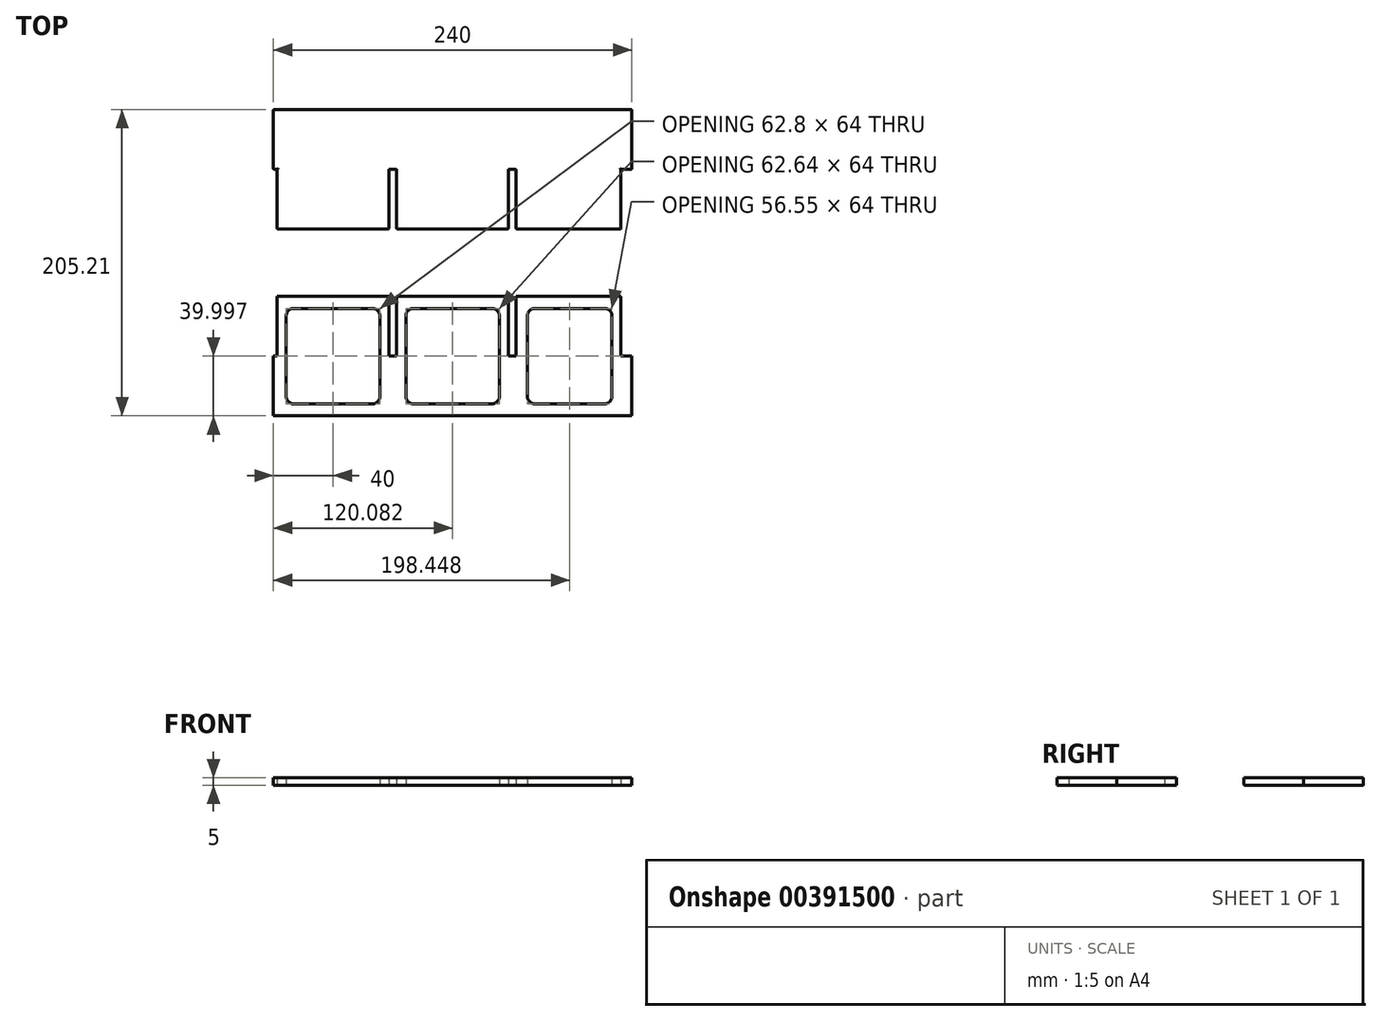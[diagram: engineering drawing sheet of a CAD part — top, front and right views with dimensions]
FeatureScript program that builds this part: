
annotation { "Feature Type Name" : "Feature", "Feature Type Description" : "" }
export const myFeature = defineFeature(function(context is Context, id is Id, definition is map)
    precondition{}
    {
        {
            var Q0;
            Q0=qCreatedBy(makeId("Top.planeOp"),FACE);
            var sketch = newSketch(context, id + "F0", { "sketchPlane" : qUnion([Q0])});
            skLineSegment(sketch, "E0.bottom", {"start": v(-120, 40) * mm, "end": v(120, 40) * mm});
            skLineSegment(sketch, "E0.top", {"start": v(-117.4, -40) * mm, "end": v(-42.6, -40) * mm});
            skLineSegment(sketch, "E0.left", {"start": v(-120, 40) * mm, "end": v(-120, 0) * mm});
            skLineSegment(sketch, "E0.right", {"start": v(120, 40) * mm, "end": v(120, 0) * mm});
            skLineSegment(sketch, "E1", {"start": v(-40, 49.5) * mm, "end": v(-40, -50.63) * mm, "construction": true});
            skLineSegment(sketch, "E2", {"start": v(-40, -50.63) * mm, "end": v(40, -50.63) * mm, "construction": true});
            skLineSegment(sketch, "E3", {"start": v(40, -50.63) * mm, "end": v(40, 54.36) * mm, "construction": true});
            skLineSegment(sketch, "E4.top", {"start": v(-42.6, 0) * mm, "end": v(-37.4, 0) * mm});
            skLineSegment(sketch, "E4.left", {"start": v(-42.6, -40) * mm, "end": v(-42.6, 0) * mm});
            skLineSegment(sketch, "E4.right", {"start": v(-37.4, -40) * mm, "end": v(-37.4, 0) * mm});
            skLineSegment(sketch, "E5.top", {"start": v(37.4, 0) * mm, "end": v(42.6, 0) * mm});
            skLineSegment(sketch, "E5.left", {"start": v(37.4, -40) * mm, "end": v(37.4, 0) * mm});
            skLineSegment(sketch, "E5.right", {"start": v(42.6, -40) * mm, "end": v(42.6, 0) * mm});
            skLineSegment(sketch, "E6.trimOffspring", {"start": v(-37.4, -40) * mm, "end": v(37.4, -40) * mm});
            skLineSegment(sketch, "E7.trimOffspring", {"start": v(42.6, -40) * mm, "end": v(112.72, -40) * mm});
            skLineSegment(sketch, "E8.top", {"start": v(-117.4, 0) * mm, "end": v(-120, 0) * mm});
            skLineSegment(sketch, "E8.left", {"start": v(-117.4, -40) * mm, "end": v(-117.4, 0) * mm});
            skLineSegment(sketch, "E9.top", {"start": v(112.72, 0) * mm, "end": v(120, 0) * mm});
            skLineSegment(sketch, "E9.left", {"start": v(112.72, -40) * mm, "end": v(112.72, 0) * mm});
            skPoint(sketch, "E10.orphan", {"position": v(-120, -40) * mm});
            skPoint(sketch, "E11.orphan", {"position": v(120, -40) * mm});
            skLineSegment(sketch, "E12", {"start": v(-148.57, -62.6) * mm, "end": v(145.2, -62.6) * mm, "construction": true});
            skLineSegment(sketch, "E13.MirrorCS", {"start": v(-117.4, -85.21) * mm, "end": v(-42.6, -85.21) * mm});
            skLineSegment(sketch, "E14.MirrorCS", {"start": v(-117.4, -85.21) * mm, "end": v(-117.4, -125.21) * mm});
            skLineSegment(sketch, "E15.MirrorCS", {"start": v(-117.4, -125.21) * mm, "end": v(-120, -125.21) * mm});
            skLineSegment(sketch, "E16.MirrorCS", {"start": v(-120, -165.21) * mm, "end": v(-120, -125.21) * mm});
            skLineSegment(sketch, "E17.MirrorCS", {"start": v(-120, -165.21) * mm, "end": v(120, -165.21) * mm});
            skLineSegment(sketch, "E18.MirrorCS", {"start": v(-42.6, -85.21) * mm, "end": v(-42.6, -125.21) * mm});
            skLineSegment(sketch, "E19.MirrorCS", {"start": v(-42.6, -125.21) * mm, "end": v(-37.4, -125.21) * mm});
            skLineSegment(sketch, "E20.MirrorCS", {"start": v(-37.4, -85.21) * mm, "end": v(37.4, -85.21) * mm});
            skLineSegment(sketch, "E21.MirrorCS", {"start": v(37.4, -85.21) * mm, "end": v(37.4, -125.21) * mm});
            skLineSegment(sketch, "E22.MirrorCS", {"start": v(42.6, -85.21) * mm, "end": v(42.6, -125.21) * mm});
            skLineSegment(sketch, "E23.MirrorCS", {"start": v(42.6, -85.21) * mm, "end": v(112.72, -85.21) * mm});
            skLineSegment(sketch, "E24.MirrorCS", {"start": v(112.72, -85.21) * mm, "end": v(112.72, -125.21) * mm});
            skLineSegment(sketch, "E25.MirrorCS", {"start": v(37.4, -125.21) * mm, "end": v(42.6, -125.21) * mm});
            skLineSegment(sketch, "E26.MirrorCS", {"start": v(-37.4, -85.21) * mm, "end": v(-37.4, -125.21) * mm});
            skLineSegment(sketch, "E27.MirrorCS", {"start": v(112.72, -125.21) * mm, "end": v(120, -125.21) * mm});
            skLineSegment(sketch, "E28.MirrorCS", {"start": v(120, -165.21) * mm, "end": v(120, -125.21) * mm});
            skLineSegment(sketch, "E29.bottom", {"start": v(-111.4, -93.21) * mm, "end": v(-48.6, -93.21) * mm});
            skLineSegment(sketch, "E29.top", {"start": v(-111.4, -157.21) * mm, "end": v(-48.6, -157.21) * mm});
            skLineSegment(sketch, "E29.left", {"start": v(-111.4, -93.21) * mm, "end": v(-111.4, -157.21) * mm});
            skLineSegment(sketch, "E29.right", {"start": v(-48.6, -93.21) * mm, "end": v(-48.6, -157.21) * mm});
            skLineSegment(sketch, "E30.bottom", {"start": v(-31.24, -93.21) * mm, "end": v(31.4, -93.21) * mm});
            skLineSegment(sketch, "E30.top", {"start": v(-31.24, -157.21) * mm, "end": v(31.4, -157.21) * mm});
            skLineSegment(sketch, "E30.left", {"start": v(-31.24, -93.21) * mm, "end": v(-31.24, -157.21) * mm});
            skLineSegment(sketch, "E30.right", {"start": v(31.4, -93.21) * mm, "end": v(31.4, -157.21) * mm});
            skLineSegment(sketch, "E31.bottom", {"start": v(50.17, -93.21) * mm, "end": v(106.72, -93.21) * mm});
            skLineSegment(sketch, "E31.top", {"start": v(50.17, -157.21) * mm, "end": v(106.72, -157.21) * mm});
            skLineSegment(sketch, "E31.left", {"start": v(50.17, -93.21) * mm, "end": v(50.17, -157.21) * mm});
            skLineSegment(sketch, "E31.right", {"start": v(106.72, -93.21) * mm, "end": v(106.72, -157.21) * mm});
            skSolve(sketch);
        }
        {
            var Q0;
            Q0=makeQuery(id+"F0.imprint","IMPRINT",FACE,{"disambiguationData":[TD([[makeQuery(id+"F0.imprint","IMPRINT",EDGE,{"derivedFrom":sQuery(id+"F0.wireOp",EDGE,"E0.bottom")}),-1.0]])]});
            var Q1;
            Q1=makeQuery(id+"F0.imprint","IMPRINT",FACE,{"disambiguationData":[TD([[makeQuery(id+"F0.imprint","IMPRINT",EDGE,{"derivedFrom":sQuery(id+"F0.wireOp",EDGE,"E13.MirrorCS")}),-1.0]])]});
            extrude(context, id + "F1", {"entities" : qUnion([Q0, Q1]), "depth" : 5 * mm});
        }
        {
            var Q0;
            Q0=makeQuery(id+"F1.opExtrude","SWEPT_EDGE",EDGE,{"disambiguationData":[OSD([sQuery(id+"F0.wireOp",EDGE,"E0.top"),sQuery(id+"F0.wireOp",EDGE,"E4.left")])]});
            var Q1;
            Q1=makeQuery(id+"F1.opExtrude","SWEPT_EDGE",EDGE,{"disambiguationData":[OSD([sQuery(id+"F0.wireOp",EDGE,"E4.right"),sQuery(id+"F0.wireOp",EDGE,"E6.trimOffspring")])]});
            var Q2;
            Q2=makeQuery(id+"F1.opExtrude","SWEPT_EDGE",EDGE,{"disambiguationData":[OSD([sQuery(id+"F0.wireOp",EDGE,"E5.left"),sQuery(id+"F0.wireOp",EDGE,"E6.trimOffspring")])]});
            var Q3;
            Q3=makeQuery(id+"F1.opExtrude","SWEPT_EDGE",EDGE,{"disambiguationData":[OSD([sQuery(id+"F0.wireOp",EDGE,"E5.right"),sQuery(id+"F0.wireOp",EDGE,"E7.trimOffspring")])]});
            var Q4;
            Q4=makeQuery(id+"F1.opExtrude","SWEPT_EDGE",EDGE,{"disambiguationData":[OSD([sQuery(id+"F0.wireOp",EDGE,"E0.top"),sQuery(id+"F0.wireOp",EDGE,"E0.left")])]});
            var Q5;
            Q5=makeQuery(id+"F1.opExtrude","SWEPT_EDGE",EDGE,{"disambiguationData":[OSD([sQuery(id+"F0.wireOp",EDGE,"E0.bottom"),sQuery(id+"F0.wireOp",EDGE,"E0.left")])]});
            var Q6;
            Q6=makeQuery(id+"F1.opExtrude","SWEPT_EDGE",EDGE,{"disambiguationData":[OSD([sQuery(id+"F0.wireOp",EDGE,"E0.bottom"),sQuery(id+"F0.wireOp",EDGE,"E0.right")])]});
            var Q7;
            Q7=makeQuery(id+"F1.opExtrude","SWEPT_EDGE",EDGE,{"disambiguationData":[OSD([sQuery(id+"F0.wireOp",EDGE,"E5.top"),sQuery(id+"F0.wireOp",EDGE,"E5.right")])]});
            var Q8;
            Q8=makeQuery(id+"F1.opExtrude","SWEPT_EDGE",EDGE,{"disambiguationData":[OSD([sQuery(id+"F0.wireOp",EDGE,"E5.top"),sQuery(id+"F0.wireOp",EDGE,"E5.left")])]});
            var Q9;
            Q9=makeQuery(id+"F1.opExtrude","SWEPT_EDGE",EDGE,{"disambiguationData":[OSD([sQuery(id+"F0.wireOp",EDGE,"E4.top"),sQuery(id+"F0.wireOp",EDGE,"E4.right")])]});
            var Q10;
            Q10=makeQuery(id+"F1.opExtrude","SWEPT_EDGE",EDGE,{"disambiguationData":[OSD([sQuery(id+"F0.wireOp",EDGE,"E4.top"),sQuery(id+"F0.wireOp",EDGE,"E4.left")])]});
            var Q11;
            Q11=makeQuery(id+"F1.opExtrude","CAP_EDGE",EDGE,{"disambiguationData":[OSD([sQuery(id+"F0.wireOp",EDGE,"E4.top")])],"isStart":true});
            var Q12;
            Q12=makeQuery(id+"F1.opExtrude","CAP_FACE",FACE,{"disambiguationData":[OSD([sQuery(id+"F0.wireOp",EDGE,"E0.bottom"),sQuery(id+"F0.wireOp",EDGE,"E0.top"),sQuery(id+"F0.wireOp",EDGE,"E0.left"),sQuery(id+"F0.wireOp",EDGE,"E0.right"),sQuery(id+"F0.wireOp",EDGE,"E4.top"),sQuery(id+"F0.wireOp",EDGE,"E4.left"),sQuery(id+"F0.wireOp",EDGE,"E4.right"),sQuery(id+"F0.wireOp",EDGE,"E5.top"),sQuery(id+"F0.wireOp",EDGE,"E5.left"),sQuery(id+"F0.wireOp",EDGE,"E5.right"),sQuery(id+"F0.wireOp",EDGE,"E6.trimOffspring"),sQuery(id+"F0.wireOp",EDGE,"E7.trimOffspring")])],"isStart":true});
            var Q13;
            Q13=makeQuery(id+"F1.opExtrude","CAP_EDGE",EDGE,{"disambiguationData":[OSD([sQuery(id+"F0.wireOp",EDGE,"E4.top")])],"isStart":false});
            var Q14;
            Q14=makeQuery(id+"F1.opExtrude","CAP_EDGE",EDGE,{"disambiguationData":[OSD([sQuery(id+"F0.wireOp",EDGE,"E5.top")])],"isStart":false});
            var Q15;
            Q15=makeQuery(id+"F1.opExtrude","SWEPT_EDGE",EDGE,{"disambiguationData":[OSD([sQuery(id+"F0.wireOp",EDGE,"E0.right"),sQuery(id+"F0.wireOp",EDGE,"E7.trimOffspring")])]});
            var Q16;
            Q16=makeQuery(id+"F1.opExtrude","CAP_EDGE",EDGE,{"disambiguationData":[OSD([sQuery(id+"F0.wireOp",EDGE,"E8.left")])],"isStart":false});
            var Q17;
            Q17=makeQuery(id+"F1.opExtrude","CAP_EDGE",EDGE,{"disambiguationData":[OSD([sQuery(id+"F0.wireOp",EDGE,"E8.top")])],"isStart":false});
            var Q18;
            Q18=makeQuery(id+"F1.opExtrude","CAP_EDGE",EDGE,{"disambiguationData":[OSD([sQuery(id+"F0.wireOp",EDGE,"E9.left")])],"isStart":false});
            var Q19;
            Q19=makeQuery(id+"F1.opExtrude","CAP_EDGE",EDGE,{"disambiguationData":[OSD([sQuery(id+"F0.wireOp",EDGE,"E9.top")])],"isStart":false});
            var Q20;
            Q20=makeQuery(id+"F1.opExtrude","CAP_EDGE",EDGE,{"disambiguationData":[OSD([sQuery(id+"F0.wireOp",EDGE,"E9.left")])],"isStart":true});
            var Q21;
            Q21=makeQuery(id+"F1.opExtrude","CAP_EDGE",EDGE,{"disambiguationData":[OSD([sQuery(id+"F0.wireOp",EDGE,"E8.left")])],"isStart":true});
            fillet(context, id + "F2", {"entities" : qUnion([Q0, Q1, Q2, Q3, Q4, Q5, Q6, Q7, Q8, Q9, Q10, Q11, Q12, Q13, Q14, Q15, Q16, Q17, Q18, Q19, Q20, Q21]), "radius" : 0.5 * mm, "tangentPropagation" : true, "allowEdgeOverflow" : false});
        }
        {
            var Q0;
            Q0=makeQuery(id+"F1.opExtrude","SWEPT_EDGE",EDGE,{"disambiguationData":[OSD([sQuery(id+"F0.wireOp",EDGE,"E29.bottom"),sQuery(id+"F0.wireOp",EDGE,"E29.left")])]});
            var Q1;
            Q1=makeQuery(id+"F1.opExtrude","SWEPT_EDGE",EDGE,{"disambiguationData":[OSD([sQuery(id+"F0.wireOp",EDGE,"E29.bottom"),sQuery(id+"F0.wireOp",EDGE,"E29.right")])]});
            var Q2;
            Q2=makeQuery(id+"F1.opExtrude","SWEPT_EDGE",EDGE,{"disambiguationData":[OSD([sQuery(id+"F0.wireOp",EDGE,"E29.top"),sQuery(id+"F0.wireOp",EDGE,"E29.left")])]});
            var Q3;
            Q3=makeQuery(id+"F1.opExtrude","SWEPT_EDGE",EDGE,{"disambiguationData":[OSD([sQuery(id+"F0.wireOp",EDGE,"E29.top"),sQuery(id+"F0.wireOp",EDGE,"E29.right")])]});
            var Q4;
            Q4=makeQuery(id+"F1.opExtrude","SWEPT_EDGE",EDGE,{"disambiguationData":[OSD([sQuery(id+"F0.wireOp",EDGE,"E31.bottom"),sQuery(id+"F0.wireOp",EDGE,"E31.right")])]});
            var Q5;
            Q5=makeQuery(id+"F1.opExtrude","SWEPT_EDGE",EDGE,{"disambiguationData":[OSD([sQuery(id+"F0.wireOp",EDGE,"E30.bottom"),sQuery(id+"F0.wireOp",EDGE,"E30.right")])]});
            var Q6;
            Q6=makeQuery(id+"F1.opExtrude","SWEPT_EDGE",EDGE,{"disambiguationData":[OSD([sQuery(id+"F0.wireOp",EDGE,"E30.top"),sQuery(id+"F0.wireOp",EDGE,"E30.right")])]});
            var Q7;
            Q7=makeQuery(id+"F1.opExtrude","SWEPT_EDGE",EDGE,{"disambiguationData":[OSD([sQuery(id+"F0.wireOp",EDGE,"E31.top"),sQuery(id+"F0.wireOp",EDGE,"E31.right")])]});
            var Q8;
            Q8=makeQuery(id+"F1.opExtrude","SWEPT_EDGE",EDGE,{"disambiguationData":[OSD([sQuery(id+"F0.wireOp",EDGE,"E31.top"),sQuery(id+"F0.wireOp",EDGE,"E31.left")])]});
            var Q9;
            Q9=makeQuery(id+"F1.opExtrude","SWEPT_EDGE",EDGE,{"disambiguationData":[OSD([sQuery(id+"F0.wireOp",EDGE,"E30.top"),sQuery(id+"F0.wireOp",EDGE,"E30.left")])]});
            var Q10;
            Q10=makeQuery(id+"F1.opExtrude","SWEPT_EDGE",EDGE,{"disambiguationData":[OSD([sQuery(id+"F0.wireOp",EDGE,"E30.bottom"),sQuery(id+"F0.wireOp",EDGE,"E30.left")])]});
            var Q11;
            Q11=makeQuery(id+"F1.opExtrude","SWEPT_EDGE",EDGE,{"disambiguationData":[OSD([sQuery(id+"F0.wireOp",EDGE,"E31.bottom"),sQuery(id+"F0.wireOp",EDGE,"E31.left")])]});
            fillet(context, id + "F3", {"entities" : qUnion([Q0, Q1, Q2, Q3, Q4, Q5, Q6, Q7, Q8, Q9, Q10, Q11]), "radius" : 5 * mm, "tangentPropagation" : true, "allowEdgeOverflow" : false});
        }
    });
